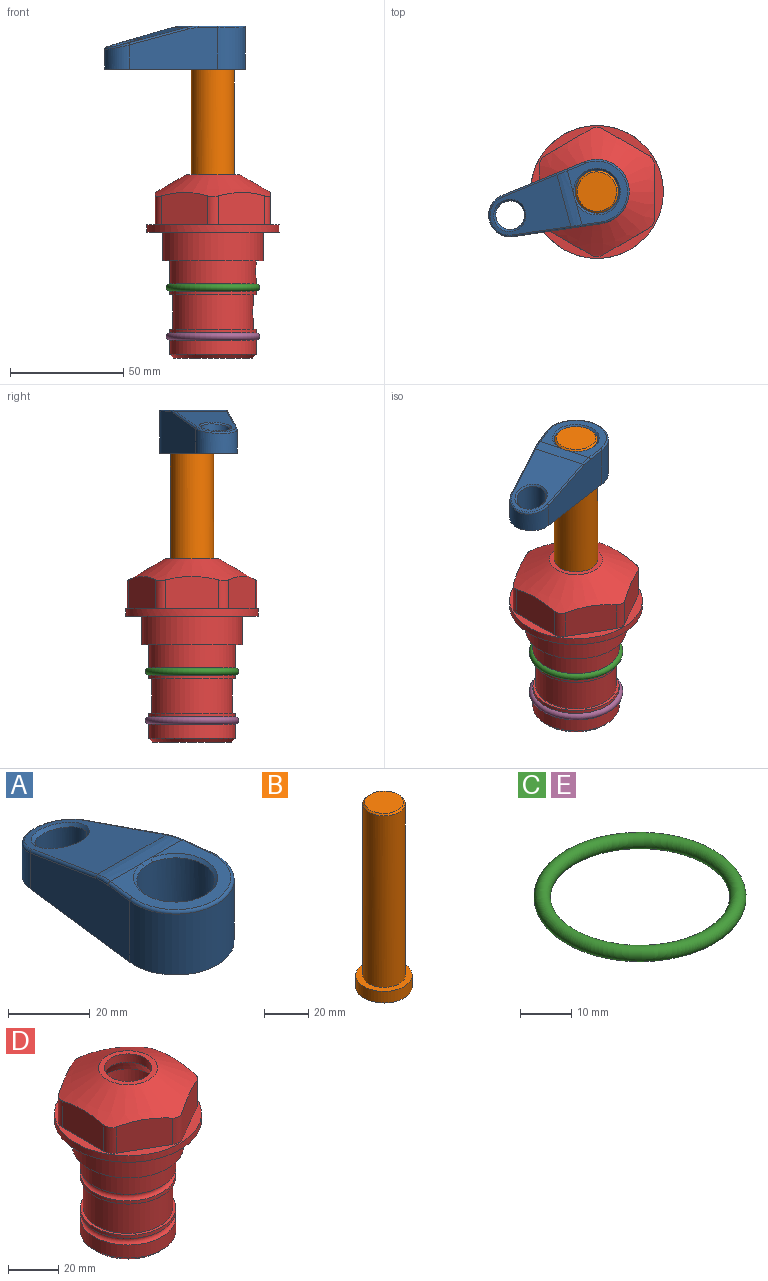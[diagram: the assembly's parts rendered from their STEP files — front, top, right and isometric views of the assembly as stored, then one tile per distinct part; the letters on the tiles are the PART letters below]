
ASSEMBLY  parts=5 mates=3
PART A: 31 faces, bbox 31.7x65.5x19.8 mm
  f0: plane 39.12x18.26mm, normal (0.99,0.12,0), area 612.2mm2, adj f1,f4,f7,f11,f13,f15
  f1: cylinder r=9.53mm len=18.91mm, axis (0,0,-1), area 296.1mm2, adj f0,f2,f7,f17
  f2: plane 39.12x18.26mm, normal (-0.99,0.12,0), area 612.2mm2, adj f1,f4,f7,f12,f14,f16
  f3: cylinder r=6.35mm len=12.7mm, axis (0,0,-1), area 362.4mm2, adj f7,f18
  f4: cylinder r=14.29mm len=28.58mm, axis (0,0,-1), area 882.2mm2, adj f0,f2,f7,f10
  f5: cylinder r=9.53mm len=19.05mm, axis (0,0,-1), area 1092.6mm2, adj f7,f19,f20
  f6: plane 26.99x23.69mm, normal (0,0,1), area 216.2mm2, adj f9,f10,f11,f12,f19
  f7: plane 63.5x28.58mm, normal (0,0,-1), area 661.8mm2, adj f0,f1,f2,f3,f4,f5,f22,f23
  f8: plane 33.52x23.6mm, normal (0,0.26,0.97), area 486mm2, adj f9,f15,f16,f17,f18
  f9: cylinder r=19.05mm len=24.72mm, axis (1,0,0), area 120.4mm2, adj f6,f8,f13,f14,f20
  f10: torus R=13.49mm, axis (0,0,1), area 59mm2, adj f4,f6,f11,f12
  f11: cylinder r=0.79mm len=8.67mm, axis (0.12,-0.99,0), area 10.8mm2, adj f0,f6,f10,f13
  f12: cylinder r=0.79mm len=8.67mm, axis (0.12,0.99,0), area 10.8mm2, adj f2,f6,f10,f14
  f13: bspline ~4.95x1.42mm, area 6.1mm2, adj f0,f9,f11,f15
  f14: bspline ~4.95x1.42mm, area 6.1mm2, adj f2,f9,f12,f16
  f15: cylinder r=0.79mm len=25.95mm, axis (0.12,-0.96,0.26), area 32.9mm2, adj f0,f8,f13,f17
  f16: cylinder r=0.79mm len=25.95mm, axis (0.12,0.96,-0.26), area 32.9mm2, adj f2,f8,f14,f17
  f17: bspline ~18.91x8.38mm, area 30mm2, adj f1,f8,f15,f16
  f18: bspline ~14.29x14.29mm, area 48.3mm2, adj f3,f8
  f19: cone r=9.53mm half-angle=45deg, axis (0,0,1), area 66.5mm2, adj f5,f6,f20
  f20: bspline ~3.22x0.96mm, area 3.5mm2, adj f5,f9,f19
  f21: plane 2.75x2.72mm, normal (0,0,-1), area 2.9mm2, adj f23,f25,f28
  f22: plane 23.05x15.88mm, normal (-0.99,-0.12,0), area 323.6mm2, adj f7,f25,f26,f27,f28,f29
  f23: plane 23.05x15.88mm, normal (0.99,-0.12,0), area 323.6mm2, adj f7,f21,f25,f27,f28,f30
  f24: cylinder r=9.53mm len=10.69mm, axis (0,0,-1), area 114.7mm2, adj f7,f27,f29,f30
  f25: cylinder r=12.7mm len=20.59mm, axis (0,0,-1), area 381.1mm2, adj f7,f21,f22,f23,f26,f28
  f26: plane 2.75x2.72mm, normal (0,0,-1), area 2.9mm2, adj f22,f25,f28
  f27: plane 19.72x18.37mm, normal (0,-0.26,-0.97), area 291.8mm2, adj f22,f23,f24,f28,f29,f30
  f28: cylinder r=15.88mm len=19.92mm, axis (1,0,0), area 54.8mm2, adj f21,f22,f23,f25,f26,f27
  f29: cylinder r=1.59mm len=11mm, axis (0,0,-1), area 34.7mm2, adj f7,f22,f24,f27
  f30: cylinder r=1.59mm len=11mm, axis (0,0,-1), area 34.7mm2, adj f7,f23,f24,f27
PART B: 6 faces, bbox 25.4x25.4x101.6 mm
  f0: plane 17.46x17.46mm, normal (0,0,1), area 239.5mm2, adj f5
  f1: plane 25.4x25.4mm, normal (0,0,-1), area 506.7mm2, adj f2
  f2: cylinder r=12.7mm len=25.4mm, axis (0,0,1), area 506.7mm2, adj f1,f3
  f3: plane 25.4x25.4mm, normal (0,0,1), area 221.7mm2, adj f2,f4
  f4: cylinder r=9.53mm len=94.46mm, axis (0,0,1), area 5653mm2, adj f3,f5
  f5: cone r=8.73mm half-angle=45deg, axis (0,0,-1), area 64.4mm2, adj f0,f4
PART C: 1 faces, bbox 44.7x44.7x3.2 mm
  f0: torus R=19.05mm, axis (0,0,1), area 1193.9mm2
PART D: 36 faces, bbox 58.7x58.7x81 mm
  f0: cylinder r=17.78mm len=35.56mm, axis (0,0,1), area 1670.8mm2, adj f23,f24,f31
  f1: cylinder r=19.05mm len=38.1mm, axis (0,0,1), area 1191.9mm2, adj f26,f27,f30
  f2: plane 58.66x58.66mm, normal (0,0,-1), area 1150.6mm2, adj f3,f28
  f3: cylinder r=29.33mm len=58.66mm, axis (0,0,-1), area 585.1mm2, adj f2,f4
  f4: plane 58.66x58.66mm, normal (0,0,1), area 475.9mm2, adj f3,f5,f6,f7,f8,f9,f10,f11
  f5: plane 20.32x14.34mm, normal (-0.5,0.87,0), area 324.4mm2, adj f4,f15,f16,f17
  f6: plane 20.32x14.34mm, normal (0.5,0.87,0), area 324.4mm2, adj f4,f14,f15,f17
  f7: plane 23.48x14.34mm, normal (1,0,0), area 324.4mm2, adj f4,f13,f14,f17
  f8: plane 20.32x14.34mm, normal (0.5,-0.87,0), area 324.4mm2, adj f4,f12,f13,f17
  f9: plane 20.32x14.34mm, normal (-0.5,-0.87,0), area 324.4mm2, adj f4,f11,f12,f17
  f10: plane 23.48x14.34mm, normal (-1,0,0), area 324.4mm2, adj f4,f11,f16,f17
  f11: cylinder r=5.08mm len=12.85mm, axis (0,0,-1), area 67.2mm2, adj f4,f9,f10,f17
  f12: cylinder r=5.08mm len=12.85mm, axis (0,0,-1), area 67.2mm2, adj f4,f8,f9,f17
  f13: cylinder r=5.08mm len=12.85mm, axis (0,0,-1), area 67.2mm2, adj f4,f7,f8,f17
  f14: cylinder r=5.08mm len=12.85mm, axis (0,0,-1), area 67.2mm2, adj f4,f6,f7,f17
  f15: cylinder r=5.08mm len=12.85mm, axis (0,0,-1), area 67.2mm2, adj f4,f5,f6,f17
  f16: cylinder r=5.08mm len=12.85mm, axis (0,0,-1), area 67.2mm2, adj f4,f5,f10,f17
  f17: cone r=11.73mm half-angle=60deg, axis (0,0,-1), area 2071.8mm2, adj f5,f6,f7,f8,f9,f10,f11,f12
  f18: plane 23.46x23.46mm, normal (0,0,1), area 147.4mm2, adj f17,f35
  f19: plane 34.93x34.93mm, normal (0,0,-1), area 958mm2, adj f29
  f20: cylinder r=19.05mm len=38.1mm, axis (0,0,1), area 760.1mm2, adj f21,f29
  f21: torus R=19.05mm, axis (0,0,1), area 565.3mm2, adj f20,f22
  f22: cylinder r=19.05mm len=38.1mm, axis (0,0,1), area 190mm2, adj f21,f23
  f23: plane 38.1x38.1mm, normal (0,0,1), area 146.9mm2, adj f0,f22
  f24: plane 38.1x38.1mm, normal (0,0,-1), area 146.9mm2, adj f0,f25
  f25: cylinder r=19.05mm len=38.1mm, axis (0,0,1), area 190mm2, adj f24,f26
  f26: torus R=19.05mm, axis (0,0,1), area 565.3mm2, adj f1,f25
  f27: plane 44.45x44.45mm, normal (0,0,-1), area 411.7mm2, adj f1,f28
  f28: cylinder r=22.23mm len=44.45mm, axis (0,0,1), area 1773.5mm2, adj f2,f27
  f29: cone r=19.05mm half-angle=45deg, axis (0,0,1), area 257.5mm2, adj f19,f20
  f30: cylinder r=3.17mm len=6.75mm, axis (-1,0,0), area 128mm2, adj f1,f33
  f31: cylinder r=3.17mm len=6.35mm, axis (-1,0,0), area 102.5mm2, adj f0,f33
  f32: plane 25.4x25.4mm, normal (0,0,1), area 506.7mm2, adj f33
  f33: cylinder r=12.7mm len=66.42mm, axis (0,0,-1), area 5236.2mm2, adj f30,f31,f32,f34
  f34: cone r=9.53mm half-angle=30deg, axis (0,0,-1), area 443.4mm2, adj f33,f35
  f35: cylinder r=9.53mm len=19.05mm, axis (0,0,-1), area 240.9mm2, adj f18,f34
PART E: same geometry as C
PLACE A rot(axis=(0,0,1),105.2deg) t=(0,0,27.55)mm
PLACE B rot(axis=(0,0,1),105.2deg) t=(0,0,27.55)mm
PLACE C at identity
PLACE D at identity fixed
PLACE E t=(0,0,-21.59)mm
MATE fastened B.f2 <-> A.f4  axis (0,0,1) through (0,0,91.05)mm
MATE fastened E.f0 <-> D.f0  axis (0,0,1) through (0,0,-46.1)mm
MATE cylindrical B.f2 <-> D.f0  axis (0,0,-1) through (0,0,-10.55)mm
